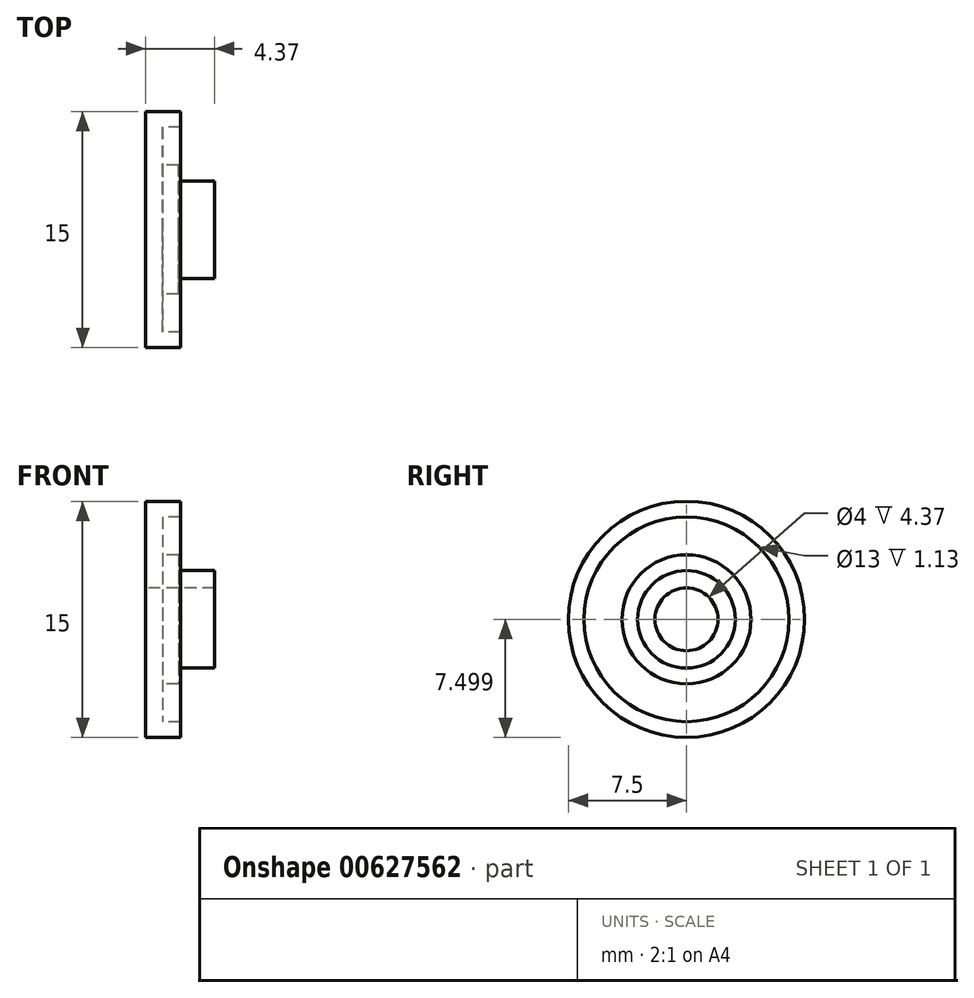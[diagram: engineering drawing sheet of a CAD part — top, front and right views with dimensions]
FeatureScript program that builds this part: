
annotation { "Feature Type Name" : "Feature", "Feature Type Description" : "" }
export const myFeature = defineFeature(function(context is Context, id is Id, definition is map)
    precondition{}
    {
        {
            var Q0;
            Q0=qCreatedBy(makeId("Front.planeOp"),FACE);
            var sketch = newSketch(context, id + "F0", { "sketchPlane" : qUnion([Q0])});
            skLineSegment(sketch, "E0", {"start": v(-38.18, 34.47) * mm, "end": v(-38.18, 28.97) * mm});
            skLineSegment(sketch, "E1", {"start": v(-38.18, 28.97) * mm, "end": v(-33.81, 28.97) * mm});
            skLineSegment(sketch, "E2", {"start": v(-33.81, 28.97) * mm, "end": v(-33.81, 30.07) * mm});
            skLineSegment(sketch, "E3", {"start": v(-33.81, 30.07) * mm, "end": v(-36.11, 30.07) * mm});
            skLineSegment(sketch, "E4", {"start": v(-36.11, 30.07) * mm, "end": v(-36.11, 31.07) * mm});
            skLineSegment(sketch, "E5", {"start": v(-36.11, 31.07) * mm, "end": v(-37.11, 31.07) * mm});
            skLineSegment(sketch, "E6", {"start": v(-37.11, 31.07) * mm, "end": v(-37.11, 33.47) * mm});
            skLineSegment(sketch, "E7", {"start": v(-37.11, 33.47) * mm, "end": v(-35.98, 33.47) * mm});
            skLineSegment(sketch, "E8", {"start": v(-35.98, 33.47) * mm, "end": v(-35.98, 34.47) * mm});
            skLineSegment(sketch, "E9", {"start": v(-35.98, 34.47) * mm, "end": v(-38.18, 34.47) * mm});
            skLineSegment(sketch, "E10", {"start": v(-39.3, 26.97) * mm, "end": v(-30.4, 26.97) * mm, "construction": true});
            skSolve(sketch);
        }
        {
            var Q0;
            Q0=makeQuery(id+"F0.imprint","IMPRINT",FACE,{"disambiguationData":[TD([[makeQuery(id+"F0.imprint","IMPRINT",EDGE,{"derivedFrom":sQuery(id+"F0.wireOp",EDGE,"E0")}),1.0]])]});
            var Q1;
            Q1=sQuery(id+"F0.wireOp",EDGE,"E10");
            revolve(context, id + "F1", {"entities" : qUnion([Q0]), "axis" : qUnion([Q1]), "revolveType" : RevolveType.FULL});
        }
    });
